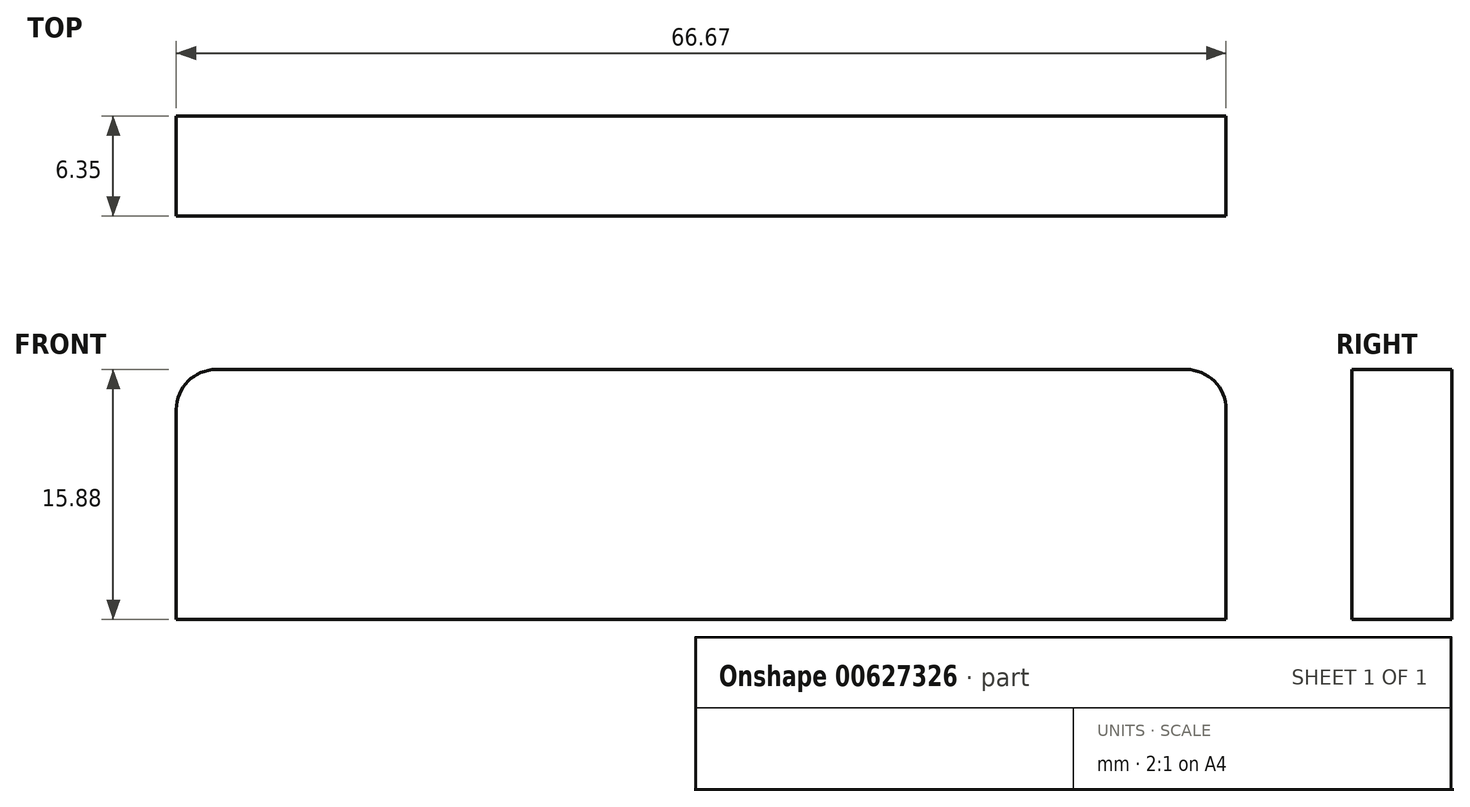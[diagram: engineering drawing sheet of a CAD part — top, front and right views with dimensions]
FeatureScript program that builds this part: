
annotation { "Feature Type Name" : "Feature", "Feature Type Description" : "" }
export const myFeature = defineFeature(function(context is Context, id is Id, definition is map)
    precondition{}
    {
        {
            var Q0;
            Q0=qCreatedBy(makeId("Front.planeOp"),FACE);
            var sketch = newSketch(context, id + "F0", { "sketchPlane" : qUnion([Q0])});
            skLineSegment(sketch, "E0.bottom", {"start": v(-96.05, 19.58) * mm, "end": v(-34.46, 19.58) * mm});
            skLineSegment(sketch, "E0.top", {"start": v(-98.6, 3.7) * mm, "end": v(-31.92, 3.7) * mm});
            skLineSegment(sketch, "E0.left", {"start": v(-98.6, 17.04) * mm, "end": v(-98.6, 3.7) * mm});
            skLineSegment(sketch, "E0.right", {"start": v(-31.92, 17.04) * mm, "end": v(-31.92, 3.7) * mm});
            skPoint(sketch, "E1.visualSharp", {"position": v(-98.6, 19.58) * mm});
            skArc(sketch, "E1.filletArc", {"start": v(-96.05, 19.58) * mm, "mid": v(-97.85, 18.83) * mm, "end": v(-98.6, 17.04) * mm});
            skPoint(sketch, "E2.visualSharp", {"position": v(-31.92, 19.58) * mm});
            skArc(sketch, "E2.filletArc", {"start": v(-31.92, 17.04) * mm, "mid": v(-32.66, 18.83) * mm, "end": v(-34.46, 19.58) * mm});
            skSolve(sketch);
        }
        {
            var Q0;
            Q0=makeQuery(id+"F0.imprint","IMPRINT",FACE,{"disambiguationData":[TD([[makeQuery(id+"F0.imprint","IMPRINT",EDGE,{"derivedFrom":sQuery(id+"F0.wireOp",EDGE,"E0.bottom")}),-1.0]])]});
            extrude(context, id + "F1", {"entities" : qUnion([Q0]), "depth" : 6.35 * mm, "offsetDistance" : 25.4 * mm});
        }
    });
